# Revit family: 5014_Cabinet for Batteries
name_source: partatom
category: Fire Alarm Devices
units: mm (PartAtom-declared; Revit-internal decimal feet)

## family parameters
Cut with Voids When Loaded = No
Host = Face
Maintain Annotation Orientation = No
OmniClass Number = 23.85.30.21
OmniClass Title = Environmental Detection/Registration
Part Type = Normal
Room Calculation Point = No
Round Connector Dimension = Use Diameter
Shared = No

## types (1)
- 5014
    Ambient Humidity = Maximum 95 % RH
    Ambient Temperature Operating = -5 to +40 °C
    Batteries = Designed for two 60-65 Ah batteries
    Default Elevation = 0 mm  [stored 0 ft]
    Depth (mm) = 175 mm  [stored 0.574147 ft]
    Description = Cabinet for batteries
    Height (mm) = 487 mm  [stored 1.59777 ft]
    Manufacturer = Panasonic
    Model = 5014
    Mounting = Wall
    Omniclass Code = 23.85.30.21.11.11.11
    Omniclass Description = Smoke Detectors
    Product Material = Metal cabinet_Aluminum-zinc – AZ150
    Type Comments = Metal cabinet intended for external CIE batteries. Cable entry (grommet) on top of the cabinet. For wall mounting.
    URL = https://www.panasonic-fire-security.com
    Uniclass 2015 Code = Pr_75_80_30_27
    Uniclass 2015 Description = Fire and smoke detector bases
    Uniformat 2010  Code = D7050
    Uniformat 2010 Description = Detection and Alarm
    Version = RVT20
    Weight = 13000 g
    Width (mm) = 420 mm  [stored 1.37795 ft]

note: [stored X ft] marks values corroborated as IEEE doubles in the binary element streams (Revit-internal decimal feet)

## geometry (parser evidence)
native form markers: Blend x2, Sweep x6
no freeform markers — native parametric forms only
